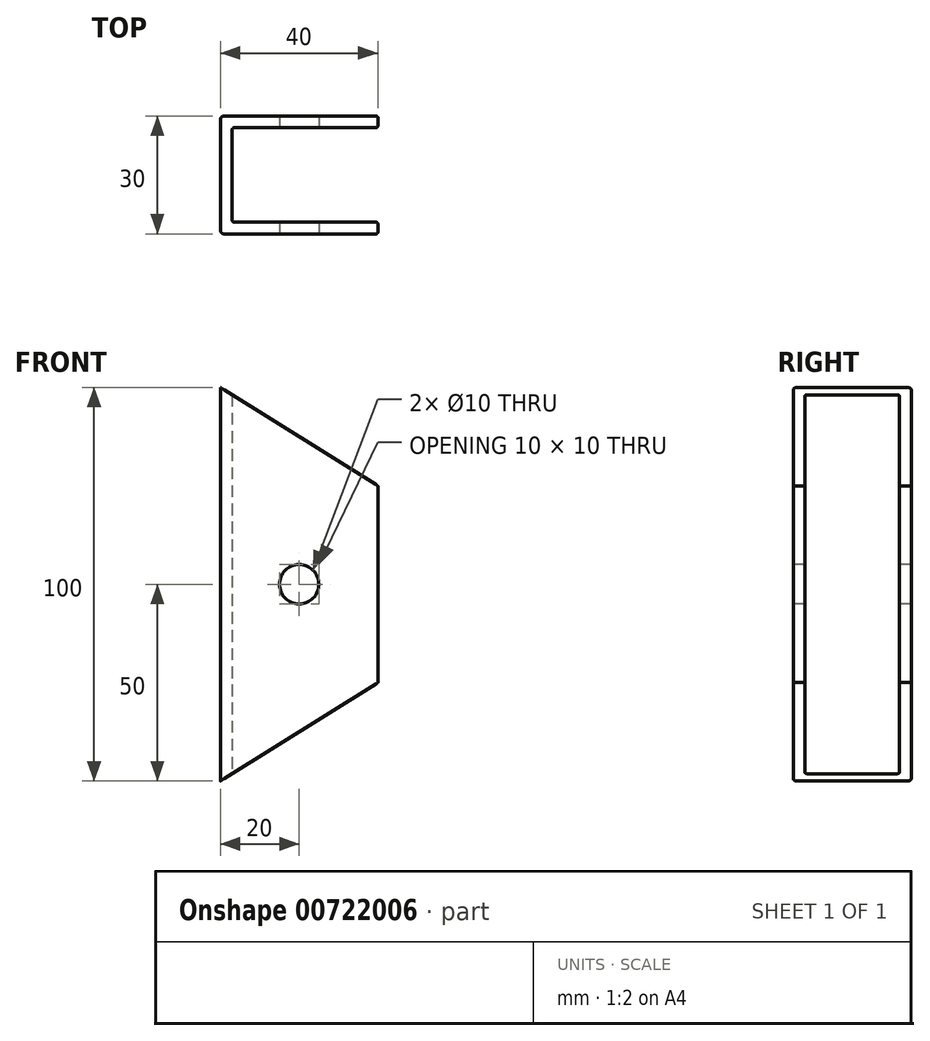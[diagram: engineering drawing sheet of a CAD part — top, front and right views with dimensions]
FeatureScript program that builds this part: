
annotation { "Feature Type Name" : "Feature", "Feature Type Description" : "" }
export const myFeature = defineFeature(function(context is Context, id is Id, definition is map)
    precondition{}
    {
        {
            var Q0;
            Q0=qCreatedBy(makeId("Top.planeOp"),FACE);
            var sketch = newSketch(context, id + "F0", { "sketchPlane" : qUnion([Q0])});
            skLineSegment(sketch, "E0", {"start": v(19.5, 15) * mm, "end": v(-19, 15) * mm});
            skLineSegment(sketch, "E1", {"start": v(-20, 14) * mm, "end": v(-20, -14) * mm});
            skLineSegment(sketch, "E2", {"start": v(-19, -15) * mm, "end": v(19.5, -15) * mm});
            skLineSegment(sketch, "E3", {"start": v(20, -14.5) * mm, "end": v(20, -12.5) * mm});
            skLineSegment(sketch, "E4", {"start": v(19.5, -12) * mm, "end": v(-16.5, -12) * mm});
            skLineSegment(sketch, "E5", {"start": v(-17, -11.5) * mm, "end": v(-17, 11.5) * mm});
            skLineSegment(sketch, "E6", {"start": v(-16.5, 12) * mm, "end": v(19.5, 12) * mm});
            skLineSegment(sketch, "E7", {"start": v(20, 12.5) * mm, "end": v(20, 14.5) * mm});
            skLineSegment(sketch, "E8", {"start": v(-16.92, 0) * mm, "end": v(14.64, 0) * mm, "construction": true});
            skLineSegment(sketch, "E9", {"start": v(0, 17.53) * mm, "end": v(0, -17.3) * mm, "construction": true});
            skPoint(sketch, "E10.visualSharp", {"position": v(-20, 15) * mm});
            skArc(sketch, "E10.filletArc", {"start": v(-19, 15) * mm, "mid": v(-19.7, 14.7) * mm, "end": v(-20, 14) * mm});
            skPoint(sketch, "E11.visualSharp", {"position": v(-20, -15) * mm});
            skArc(sketch, "E11.filletArc", {"start": v(-20, -14) * mm, "mid": v(-19.7, -14.7) * mm, "end": v(-19, -15) * mm});
            skPoint(sketch, "E12.visualSharp", {"position": v(20, 15) * mm});
            skArc(sketch, "E12.filletArc", {"start": v(20, 14.5) * mm, "mid": v(19.85, 14.85) * mm, "end": v(19.5, 15) * mm});
            skPoint(sketch, "E13.visualSharp", {"position": v(20, 12) * mm});
            skArc(sketch, "E13.filletArc", {"start": v(19.5, 12) * mm, "mid": v(19.85, 12.15) * mm, "end": v(20, 12.5) * mm});
            skPoint(sketch, "E14.visualSharp", {"position": v(-17, 12) * mm});
            skArc(sketch, "E14.filletArc", {"start": v(-16.5, 12) * mm, "mid": v(-16.85, 11.85) * mm, "end": v(-17, 11.5) * mm});
            skPoint(sketch, "E15.visualSharp", {"position": v(20, -12) * mm});
            skArc(sketch, "E15.filletArc", {"start": v(20, -12.5) * mm, "mid": v(19.85, -12.15) * mm, "end": v(19.5, -12) * mm});
            skPoint(sketch, "E16.visualSharp", {"position": v(20, -15) * mm});
            skArc(sketch, "E16.filletArc", {"start": v(19.5, -15) * mm, "mid": v(19.85, -14.85) * mm, "end": v(20, -14.5) * mm});
            skPoint(sketch, "E17.visualSharp", {"position": v(-17, -12) * mm});
            skArc(sketch, "E17.filletArc", {"start": v(-17, -11.5) * mm, "mid": v(-16.85, -11.85) * mm, "end": v(-16.5, -12) * mm});
            skSolve(sketch);
        }
        {
            var Q0;
            Q0=makeQuery(id+"F0.imprint","IMPRINT",FACE,{"disambiguationData":[TD([[makeQuery(id+"F0.imprint","IMPRINT",EDGE,{"derivedFrom":sQuery(id+"F0.wireOp",EDGE,"E0")}),1.0]])]});
            extrude(context, id + "F1", {"entities" : qUnion([Q0]), "depth" : 50 * mm, "offsetDistance" : 25 * mm, "hasSecondDirection" : true, "secondDirectionOppositeDirection" : true, "secondDirectionDepth" : 50 * mm});
        }
        {
            var Q0;
            Q0=qCreatedBy(makeId("Front.planeOp"),FACE);
            var sketch = newSketch(context, id + "F2", { "sketchPlane" : qUnion([Q0])});
            skLineSegment(sketch, "E18", {"start": v(-24, 0) * mm, "end": v(26.15, 0) * mm, "construction": true});
            skLineSegment(sketch, "E19", {"start": v(-20, 50) * mm, "end": v(20, 25) * mm});
            skLineSegment(sketch, "E20", {"start": v(20, 25) * mm, "end": v(20, 50) * mm});
            skLineSegment(sketch, "E21", {"start": v(20, 50) * mm, "end": v(-20, 50) * mm});
            skLineSegment(sketch, "E22.MirrorCS", {"start": v(-20, -50) * mm, "end": v(20, -25) * mm});
            skLineSegment(sketch, "E23.MirrorCS", {"start": v(20, -25) * mm, "end": v(20, -50) * mm});
            skLineSegment(sketch, "E24.MirrorCS", {"start": v(20, -50) * mm, "end": v(-20, -50) * mm});
            skCircle(sketch, "E25", {"center": v(0, 0) * mm, "radius": 5 * mm});
            skSolve(sketch);
        }
        {
            var Q0;
            Q0=makeQuery(id+"F2.imprint","IMPRINT",FACE,{"disambiguationData":[TD([[makeQuery(id+"F2.imprint","IMPRINT",EDGE,{"derivedFrom":sQuery(id+"F2.wireOp",EDGE,"E19")}),1.0]])]});
            var Q1;
            Q1=makeQuery(id+"F2.imprint","IMPRINT",FACE,{"disambiguationData":[TD([[makeQuery(id+"F2.imprint","IMPRINT",EDGE,{"derivedFrom":sQuery(id+"F2.wireOp",EDGE,"E22.MirrorCS")}),-1.0]])]});
            var Q2;
            Q2=makeQuery(id+"F2.imprint","IMPRINT",FACE,{"disambiguationData":[TD([[makeQuery(id+"F2.imprint","IMPRINT",EDGE,{"derivedFrom":sQuery(id+"F2.wireOp",EDGE,"E25")}),1.0]])]});
            extrude(context, id + "F3", {"entities" : qUnion([Q0, Q1, Q2]), "operationType" : NewBodyOperationType.REMOVE, "oppositeDirection" : true, "depth" : 25 * mm, "offsetDistance" : 25 * mm, "hasSecondDirection" : true, "secondDirectionOppositeDirection" : false, "secondDirectionDepth" : 25 * mm});
        }
    });
